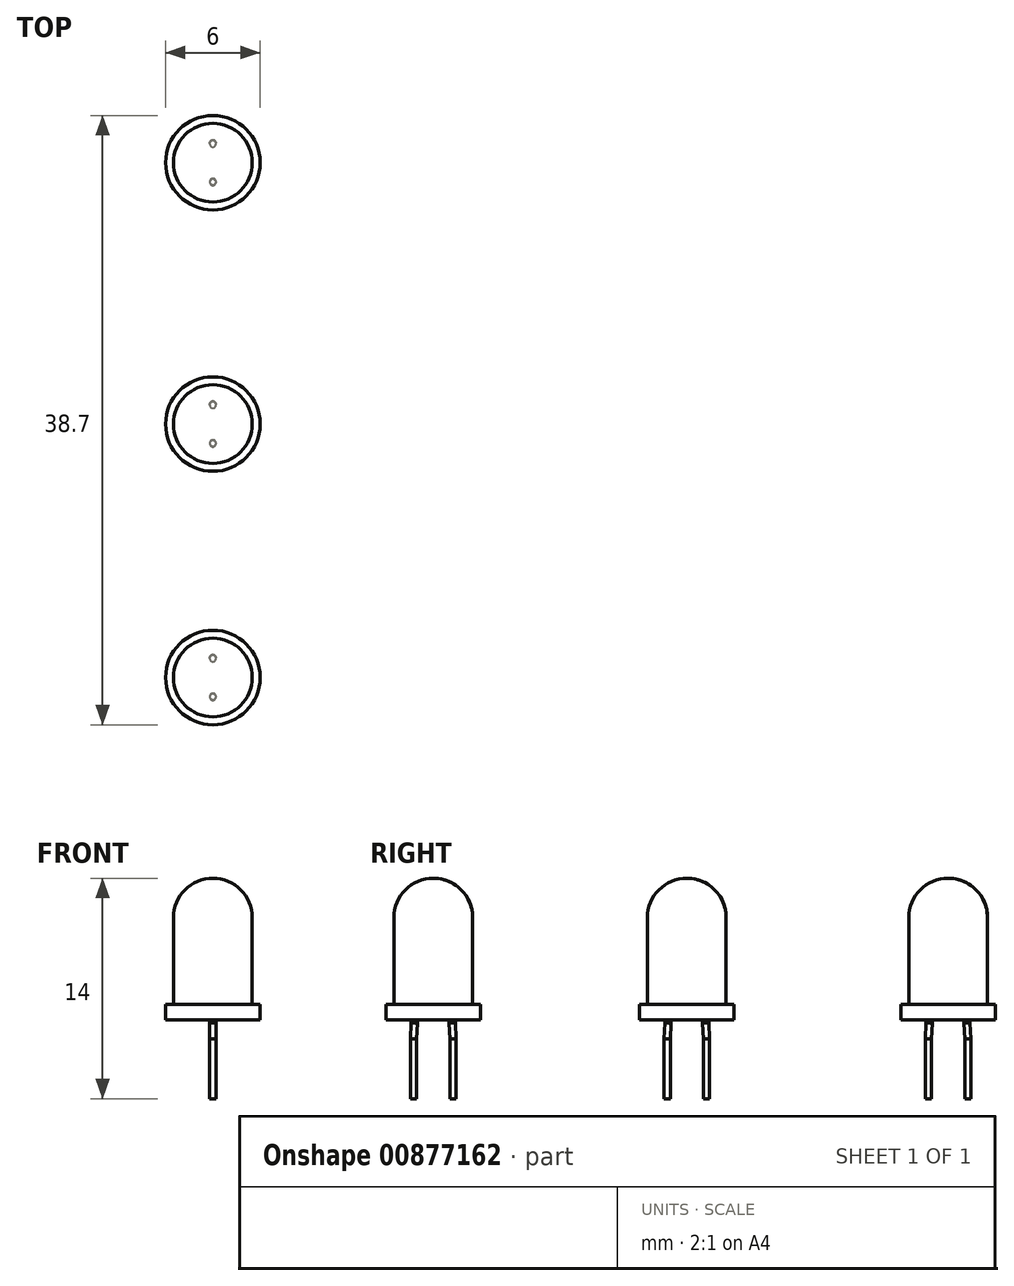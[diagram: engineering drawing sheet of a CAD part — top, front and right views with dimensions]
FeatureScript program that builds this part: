
annotation { "Feature Type Name" : "Feature", "Feature Type Description" : "" }
export const myFeature = defineFeature(function(context is Context, id is Id, definition is map)
    precondition{}
    {
        {
            var Q0;
            Q0=qCreatedBy(makeId("Right.planeOp"),FACE);
            var sketch = newSketch(context, id + "F0", { "sketchPlane" : qUnion([Q0])});
            skCircle(sketch, "E0", {"center": v(0, 6.5) * mm, "radius": 2.5 * mm});
            skLineSegment(sketch, "E1", {"start": v(2.5, 6.5) * mm, "end": v(2.5, 1) * mm});
            skLineSegment(sketch, "E2", {"start": v(2.5, 1) * mm, "end": v(3, 1) * mm});
            skLineSegment(sketch, "E3", {"start": v(3, 1) * mm, "end": v(3, 0) * mm});
            skLineSegment(sketch, "E4", {"start": v(3, 0) * mm, "end": v(0, 0) * mm});
            skLineSegment(sketch, "E5", {"start": v(0, 6.5) * mm, "end": v(0, 0) * mm});
            skLineSegment(sketch, "E6", {"start": v(0, 6.5) * mm, "end": v(0, 9) * mm});
            skSolve(sketch);
        }
        {
            var Q0;
            {var subQ0=sQuery(id+"F0.wireOp",EDGE,"E1");Q0=makeQuery(id+"F0.imprint","IMPRINT",FACE,{"disambiguationData":[TD([[makeQuery(id+"F0.imprint","IMPRINT",EDGE,{"derivedFrom":subQ0}),-1.0]])]});}
            var Q1;
            {var subQ2=sQuery(id+"F0.wireOp",EDGE,"E6");Q1=makeQuery(id+"F0.imprint","IMPRINT",FACE,{"disambiguationData":[TD([[makeQuery(id+"F0.imprint","IMPRINT",EDGE,{"derivedFrom":subQ2}),-1.0]])]});}
            var Q2;
            Q2=sQuery(id+"F0.wireOp",EDGE,"E5");
            revolve(context, id + "F1", {"surfaceOperationType" : NewSurfaceOperationType.NEW, "entities" : qUnion([Q0, Q1]), "axis" : qUnion([Q2]), "revolveType" : RevolveType.FULL});
        }
        {
            var Q0;
            Q0=qCreatedBy(makeId("Right.planeOp"),FACE);
            var sketch = newSketch(context, id + "F2", { "sketchPlane" : qUnion([Q0])});
            skLineSegment(sketch, "E7", {"start": v(1.2, 0) * mm, "end": v(1.2, -0.2) * mm});
            skLineSegment(sketch, "E8", {"start": v(-1.2, 0) * mm, "end": v(-1.2, -0.2) * mm});
            skLineSegment(sketch, "E9", {"start": v(-1.25, -1.2) * mm, "end": v(-1.25, -5) * mm});
            skLineSegment(sketch, "E10", {"start": v(1.25, -1.2) * mm, "end": v(1.25, -5) * mm});
            skLineSegment(sketch, "E11", {"start": v(-1.2, 0) * mm, "end": v(1.2, 0) * mm, "construction": true});
            skLineSegment(sketch, "E12", {"start": v(0, 0) * mm, "end": v(0, -5) * mm, "construction": true});
            skLineSegment(sketch, "E13", {"start": v(0, -5) * mm, "end": v(1.25, -5) * mm, "construction": true});
            skLineSegment(sketch, "E14", {"start": v(0, -5) * mm, "end": v(-1.25, -5) * mm, "construction": true});
            skLineSegment(sketch, "E15", {"start": v(-1.2, -0.2) * mm, "end": v(-1.25, -1.2) * mm});
            skLineSegment(sketch, "E16", {"start": v(1.2, -0.2) * mm, "end": v(1.25, -1.2) * mm});
            skSolve(sketch);
        }
        {
            var Q0;
            Q0=makeQuery(id+"F1.opRevolve","SWEPT_FACE",FACE,{"disambiguationData":[OSD([sQuery(id+"F0.wireOp",EDGE,"E4")])]});
            var sketch = newSketch(context, id + "F3", { "sketchPlane" : qUnion([Q0])});
            skCircle(sketch, "E17", {"center": v(0, -1.2) * mm, "radius": 0.2 * mm});
            skSolve(sketch);
        }
        {
            var Q0;
            Q0=makeQuery(id+"F3.imprint","IMPRINT",FACE,{"disambiguationData":[TD([[makeQuery(id+"F3.imprint","IMPRINT",EDGE,{"derivedFrom":sQuery(id+"F3.wireOp",EDGE,"E17")}),1.0]])]});
            var Q1;
            Q1=sQuery(id+"F2.wireOp",EDGE,"E7");
            var Q2;
            Q2=sQuery(id+"F2.wireOp",EDGE,"E16");
            var Q3;
            Q3=sQuery(id+"F2.wireOp",EDGE,"E10");
            sweep(context, id + "F4", {"profiles" : qUnion([Q0]), "path" : qUnion([Q1, Q2, Q3])});
        }
        {
            var Q0;
            Q0=makeQuery(id+"F4.opSweep","SWEPT_BODY",BODY,{"disambiguationData":[OSD([sQuery(id+"F2.wireOp",EDGE,"E10"),sQuery(id+"F3.wireOp",EDGE,"E17")])]});
            var Q1;
            Q1=qCreatedBy(makeId("Front.planeOp"),FACE);
            mirror(context, id + "F5", {"operationType" : NewBodyOperationType.ADD, "entities" : qUnion([Q0]), "mirrorPlane" : qUnion([Q1])});
        }
        {
            var Q0;
            Q0=makeQuery(id+"F1.opRevolve","SWEPT_BODY",BODY,{"disambiguationData":[OSD([sQuery(id+"F0.wireOp",EDGE,"E0"),sQuery(id+"F0.wireOp",EDGE,"E1"),sQuery(id+"F0.wireOp",EDGE,"E2"),sQuery(id+"F0.wireOp",EDGE,"E3"),sQuery(id+"F0.wireOp",EDGE,"E4"),sQuery(id+"F0.wireOp",EDGE,"E5"),sQuery(id+"F0.wireOp",EDGE,"E6")])]});
            transform(context, id + "F6", {"entities" : qUnion([Q0]), "transformType" : TransformType.TRANSLATION_3D, "dx" : 0 * mm, "dy" : 16.1 * mm, "dz" : 0 * mm, "makeCopy" : true});
        }
        {
            var Q0;
            Q0=makeQuery(id+"F6.opPattern","COPY",BODY,{"derivedFrom":makeQuery(id+"F1.opRevolve","SWEPT_BODY",BODY,{"disambiguationData":[OSD([sQuery(id+"F0.wireOp",EDGE,"E0"),sQuery(id+"F0.wireOp",EDGE,"E1"),sQuery(id+"F0.wireOp",EDGE,"E2"),sQuery(id+"F0.wireOp",EDGE,"E3"),sQuery(id+"F0.wireOp",EDGE,"E4"),sQuery(id+"F0.wireOp",EDGE,"E5"),sQuery(id+"F0.wireOp",EDGE,"E6")])]}),"instanceName":"1"});
            transform(context, id + "F7", {"entities" : qUnion([Q0]), "transformType" : TransformType.TRANSLATION_3D, "dx" : 0 * mm, "dy" : 16.6 * mm, "dz" : 0 * mm, "makeCopy" : true});
        }
    });
